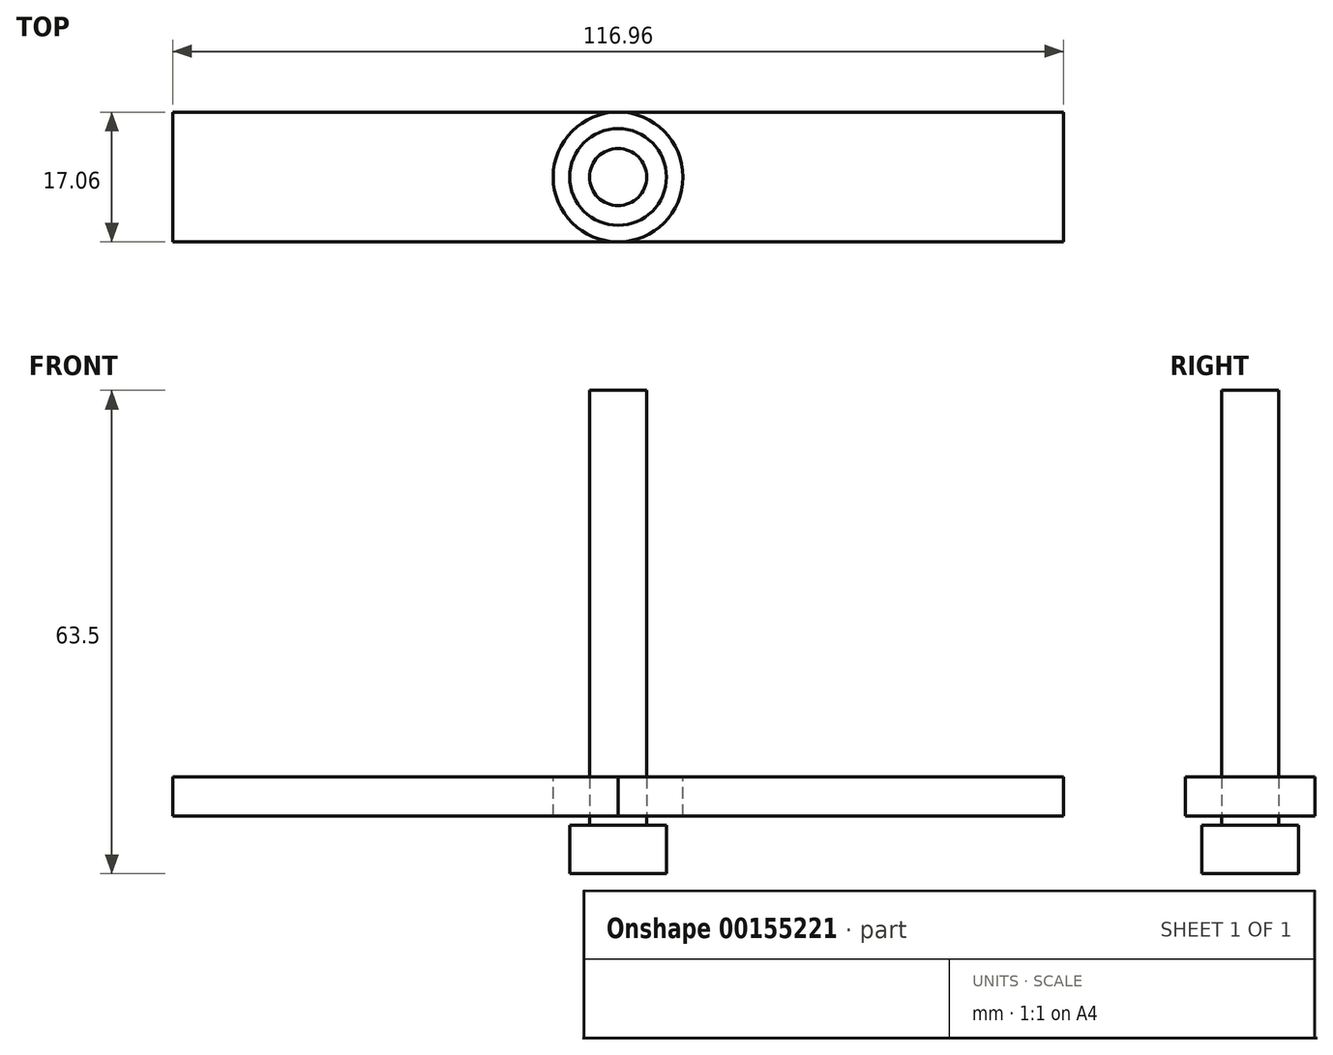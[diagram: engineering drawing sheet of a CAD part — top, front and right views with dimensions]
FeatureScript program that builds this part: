
annotation { "Feature Type Name" : "Feature", "Feature Type Description" : "" }
export const myFeature = defineFeature(function(context is Context, id is Id, definition is map)
    precondition{}
    {
        {
            var Q0;
            Q0=qCreatedBy(makeId("Top.planeOp"),FACE);
            var sketch = newSketch(context, id + "F0", { "sketchPlane" : qUnion([Q0])});
            skCircle(sketch, "E0", {"center": v(0, 0) * mm, "radius": 6.35 * mm});
            skSolve(sketch);
        }
        {
            var Q0;
            Q0=makeQuery(id+"F0.imprint","IMPRINT",FACE,{"disambiguationData":[TD([[makeQuery(id+"F0.imprint","IMPRINT",EDGE,{"derivedFrom":sQuery(id+"F0.wireOp",EDGE,"E0")}),1.0]])]});
            extrude(context, id + "F1", {"entities" : qUnion([Q0]), "depth" : 6.35 * mm});
        }
        {
            var Q0;
            Q0=makeQuery(id+"F1.opExtrude","CAP_FACE",FACE,{"disambiguationData":[OSD([sQuery(id+"F0.wireOp",EDGE,"E0")])],"isStart":false});
            var sketch = newSketch(context, id + "F2", { "sketchPlane" : qUnion([Q0])});
            skCircle(sketch, "E1", {"center": v(0, 0) * mm, "radius": 3.75 * mm});
            skSolve(sketch);
        }
        {
            var Q0;
            Q0=makeQuery(id+"F2.imprint","IMPRINT",FACE,{"disambiguationData":[TD([[makeQuery(id+"F2.imprint","IMPRINT",EDGE,{"derivedFrom":sQuery(id+"F2.wireOp",EDGE,"E1")}),1.0]])]});
            extrude(context, id + "F3", {"entities" : qUnion([Q0]), "operationType" : NewBodyOperationType.ADD, "depth" : 57.15 * mm});
        }
        {
            var Q0;
            Q0=qCreatedBy(makeId("Top.planeOp"),FACE);
            cPlane(context, id + "F4", {"entities" : qUnion([Q0]), "cplaneType" : CPlaneType.OFFSET, "offset" : 12.7 * mm, "width" : 0.17 * yard, "height" : 0.17 * yard});
        }
        {
            var Q0;
            Q0=qCreatedBy(id+"F4.planeOp",FACE);
            var sketch = newSketch(context, id + "F5", { "sketchPlane" : qUnion([Q0])});
            skLineSegment(sketch, "E2.bottom", {"start": v(58.48, -8.53) * mm, "end": v(-58.48, -8.53) * mm});
            skLineSegment(sketch, "E2.top", {"start": v(58.48, 8.53) * mm, "end": v(-58.48, 8.53) * mm});
            skLineSegment(sketch, "E2.left", {"start": v(58.48, -8.53) * mm, "end": v(58.48, 8.53) * mm});
            skLineSegment(sketch, "E2.right", {"start": v(-58.48, -8.53) * mm, "end": v(-58.48, 8.53) * mm});
            skPoint(sketch, "E2.middle", {"position": v(0, 0) * mm});
            skCircle(sketch, "E3", {"center": v(0, 0) * mm, "radius": 8.53 * mm});
            skSolve(sketch);
        }
        {
            var Q0;
            {var subQ0=sQuery(id+"F5.wireOp",EDGE,"E2.left");Q0=makeQuery(id+"F5.imprint","IMPRINT",FACE,{"disambiguationData":[TD([[makeQuery(id+"F5.imprint","IMPRINT",EDGE,{"derivedFrom":subQ0}),1.0]])]});}
            var Q1;
            {var subQ0=sQuery(id+"F5.wireOp",EDGE,"E2.right");Q1=makeQuery(id+"F5.imprint","IMPRINT",FACE,{"disambiguationData":[TD([[makeQuery(id+"F5.imprint","IMPRINT",EDGE,{"derivedFrom":subQ0}),-1.0]])]});}
            extrude(context, id + "F6", {"entities" : qUnion([Q0, Q1]), "oppositeDirection" : true, "depth" : 0 * yard});
        }
    });
